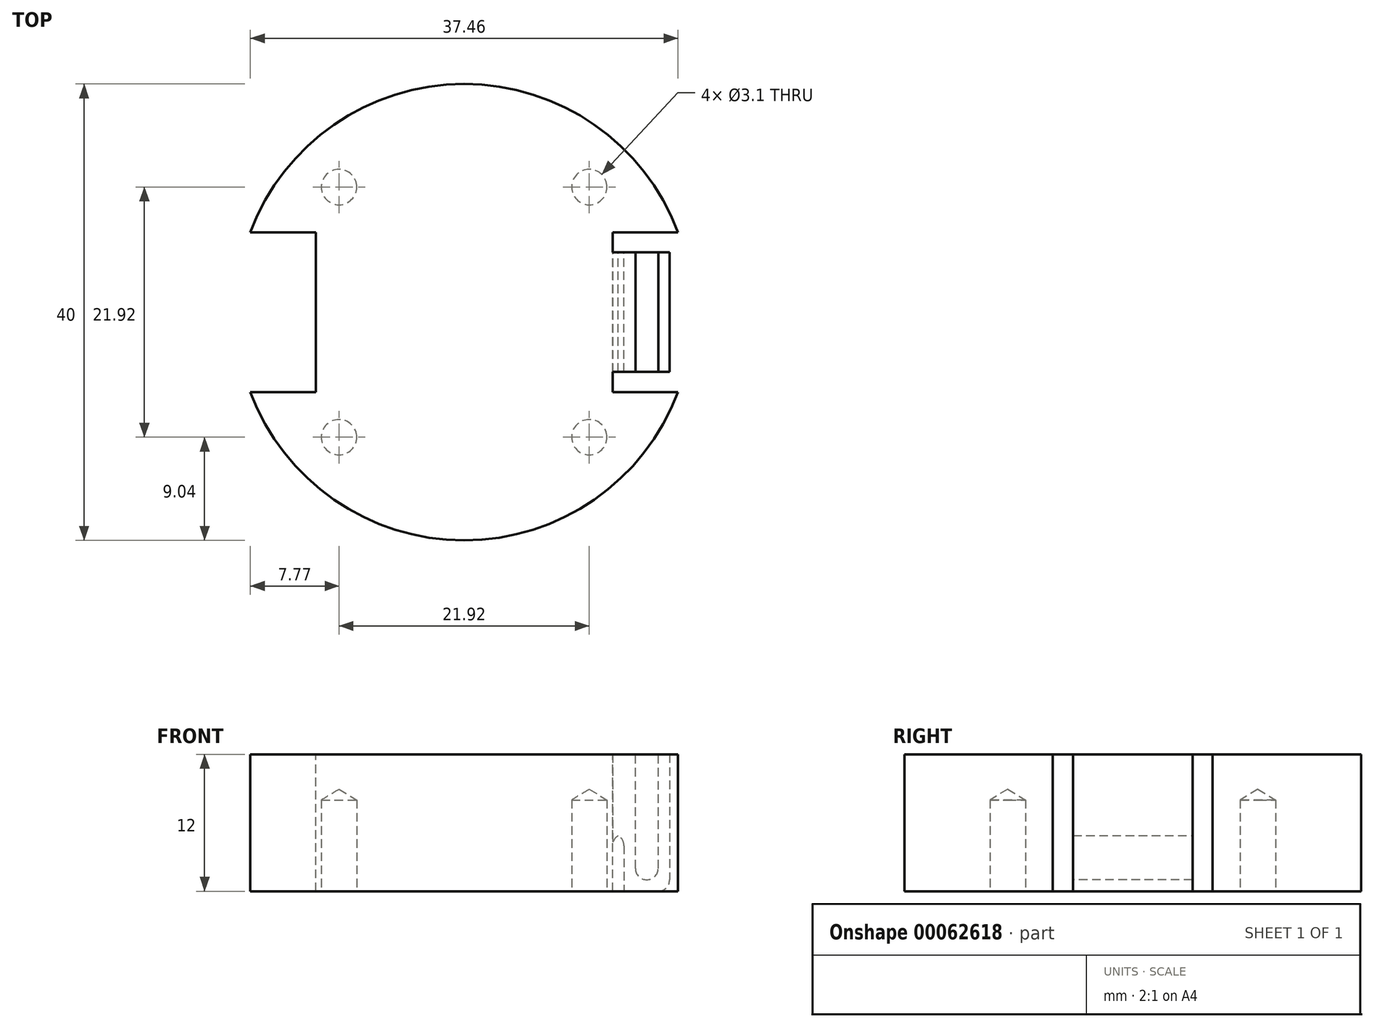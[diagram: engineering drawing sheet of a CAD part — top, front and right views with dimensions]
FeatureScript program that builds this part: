
annotation { "Feature Type Name" : "Feature", "Feature Type Description" : "" }
export const myFeature = defineFeature(function(context is Context, id is Id, definition is map)
    precondition{}
    {
        {
            var Q0;
            Q0=qCreatedBy(makeId("Top.planeOp"),FACE);
            var sketch = newSketch(context, id + "F0", { "sketchPlane" : qUnion([Q0])});
            skCircle(sketch, "E0", {"center": v(0, 0) * mm, "radius": 20 * mm});
            skSolve(sketch);
        }
        {
            var Q0;
            Q0=makeQuery(id+"F0.imprint","IMPRINT",FACE,{"disambiguationData":[TD([[makeQuery(id+"F0.imprint","IMPRINT",EDGE,{"derivedFrom":sQuery(id+"F0.wireOp",EDGE,"E0")}),1.0]])]});
            extrude(context, id + "F1", {"entities" : qUnion([Q0]), "depth" : 12 * mm});
        }
        {
            var Q0;
            Q0=makeQuery(id+"F1.opExtrude","CAP_FACE",FACE,{"disambiguationData":[OSD([sQuery(id+"F0.wireOp",EDGE,"E0")])],"isStart":true});
            var sketch = newSketch(context, id + "F2", { "sketchPlane" : qUnion([Q0])});
            skLineSegment(sketch, "E1", {"start": v(0, 0) * mm, "end": v(14.14, 14.14) * mm, "construction": true});
            skCircle(sketch, "E2.cCircle", {"center": v(0, 0) * mm, "radius": 15.5 * mm, "construction": true});
            skLineSegment(sketch, "E2.0", {"start": v(10.96, 10.96) * mm, "end": v(10.96, -10.96) * mm, "construction": true});
            skLineSegment(sketch, "E2.1", {"start": v(10.96, -10.96) * mm, "end": v(-10.96, -10.96) * mm, "construction": true});
            skLineSegment(sketch, "E2.2", {"start": v(-10.96, -10.96) * mm, "end": v(-10.96, 10.96) * mm, "construction": true});
            skLineSegment(sketch, "E2.3", {"start": v(-10.96, 10.96) * mm, "end": v(10.96, 10.96) * mm, "construction": true});
            skSolve(sketch);
        }
        {
            var Q0;
            Q0=sQuery(id+"F2.wireOp",VERTEX,"E2.3.start");
            var Q1;
            Q1=sQuery(id+"F2.wireOp",VERTEX,"E2.2.start");
            var Q2;
            Q2=sQuery(id+"F2.wireOp",VERTEX,"E2.1.start");
            var Q3;
            Q3=sQuery(id+"F2.wireOp",VERTEX,"E2.0.start");
            var Q4;
            Q4=makeQuery(id+"F1.opExtrude","SWEPT_BODY",BODY,{"disambiguationData":[OSD([sQuery(id+"F0.wireOp",EDGE,"E0")])]});
            hole(context, id + "F3", {"style" : HoleStyle.SIMPLE, "holeDiameter" : 3.1 * mm, "endStyle" : HoleEndStyle.BLIND, "holeDepth" : 8 * mm, "locations" : qUnion([Q0, Q1, Q2, Q3]), "scope" : qUnion([Q4])});
        }
        {
            var Q0;
            Q0=makeQuery(id+"F1.opExtrude","CAP_FACE",FACE,{"disambiguationData":[OSD([sQuery(id+"F0.wireOp",EDGE,"E0")])],"isStart":false});
            var sketch = newSketch(context, id + "F4", { "sketchPlane" : qUnion([Q0])});
            skLineSegment(sketch, "E3.rect.bottom", {"start": v(13, 7) * mm, "end": v(20, 7) * mm});
            skLineSegment(sketch, "E3.rect.top", {"start": v(13, -7) * mm, "end": v(20, -7) * mm});
            skLineSegment(sketch, "E3.rect.left", {"start": v(13, 7) * mm, "end": v(13, -7) * mm});
            skLineSegment(sketch, "E3.rect.right", {"start": v(20, 7) * mm, "end": v(20, -7) * mm});
            skPoint(sketch, "E3.rect.middle", {"position": v(16.5, 0) * mm});
            skLineSegment(sketch, "E4.rect.bottom", {"start": v(-13, 7) * mm, "end": v(-20, 7) * mm});
            skLineSegment(sketch, "E4.rect.top", {"start": v(-13, -7) * mm, "end": v(-20, -7) * mm});
            skLineSegment(sketch, "E4.rect.left", {"start": v(-13, 7) * mm, "end": v(-13, -7) * mm});
            skLineSegment(sketch, "E4.rect.right", {"start": v(-20, 7) * mm, "end": v(-20, -7) * mm});
            skPoint(sketch, "E4.rect.middle", {"position": v(-16.5, 0) * mm});
            skSolve(sketch);
        }
        {
            var Q0;
            {var subQ0=sQuery(id+"F4.wireOp",EDGE,"E3.rect.left");Q0=makeQuery(id+"F4.imprint","IMPRINT",FACE,{"disambiguationData":[TD([[makeQuery(id+"F4.imprint","IMPRINT",EDGE,{"derivedFrom":subQ0}),-1.0]])]});}
            extrude(context, id + "F5", {"entities" : qUnion([Q0]), "operationType" : NewBodyOperationType.INTERSECT, "endBound" : BoundingType.THROUGH_ALL, "oppositeDirection" : true, "depth" : 25 * mm});
        }
        {
            var Q0;
            Q0=qCreatedBy(makeId("Top.planeOp"),FACE);
            var sketch = newSketch(context, id + "F6", { "sketchPlane" : qUnion([Q0])});
            skLineSegment(sketch, "E5.rect.bottom", {"start": v(13, 5.23) * mm, "end": v(18, 5.23) * mm});
            skLineSegment(sketch, "E5.rect.top", {"start": v(13, -5.23) * mm, "end": v(18, -5.23) * mm});
            skLineSegment(sketch, "E5.rect.left", {"start": v(13, 5.23) * mm, "end": v(13, -5.23) * mm});
            skLineSegment(sketch, "E5.rect.right", {"start": v(18, 5.23) * mm, "end": v(18, -5.23) * mm});
            skPoint(sketch, "E5.rect.middle", {"position": v(15.5, 0) * mm});
            skSolve(sketch);
        }
        {
            var Q0;
            Q0=makeQuery(id+"F6.imprint","IMPRINT",FACE,{"disambiguationData":[TD([[makeQuery(id+"F6.imprint","IMPRINT",EDGE,{"derivedFrom":sQuery(id+"F6.wireOp",EDGE,"E5.rect.bottom")}),-1.0]])]});
            extrude(context, id + "F7", {"entities" : qUnion([Q0]), "operationType" : NewBodyOperationType.ADD, "depth" : 12 * mm});
        }
        {
            var Q0;
            {var subQ4=sQuery(id+"F4.wireOp",EDGE,"E3.rect.left");Q0=makeQuery(id+"F4.imprint","IMPRINT",FACE,{"disambiguationData":[TD([[makeQuery(id+"F4.imprint","IMPRINT",EDGE,{"derivedFrom":subQ4}),-1.0]])]});}
            var sketch = newSketch(context, id + "F8", { "sketchPlane" : qUnion([Q0])});
            skLineSegment(sketch, "E6.bottom", {"start": v(15, 5.23) * mm, "end": v(17, 5.23) * mm});
            skLineSegment(sketch, "E6.top", {"start": v(15, -5.23) * mm, "end": v(17, -5.23) * mm});
            skLineSegment(sketch, "E6.left", {"start": v(15, 5.23) * mm, "end": v(15, -5.23) * mm});
            skLineSegment(sketch, "E6.right", {"start": v(17, 5.23) * mm, "end": v(17, -5.23) * mm});
            skSolve(sketch);
        }
        {
            var Q0;
            Q0=makeQuery(id+"F8.imprint","IMPRINT",FACE,{"disambiguationData":[TD([[makeQuery(id+"F8.imprint","IMPRINT",EDGE,{"derivedFrom":sQuery(id+"F8.wireOp",EDGE,"E6.bottom")}),-1.0]])]});
            extrude(context, id + "F9", {"entities" : qUnion([Q0]), "operationType" : NewBodyOperationType.REMOVE, "oppositeDirection" : true, "depth" : 11 * mm});
        }
        {
            var Q0;
            Q0=qCreatedBy(makeId("Top.planeOp"),FACE);
            var sketch = newSketch(context, id + "F10", { "sketchPlane" : qUnion([Q0])});
            skLineSegment(sketch, "E7.bottom", {"start": v(13, -5.23) * mm, "end": v(14, -5.23) * mm});
            skLineSegment(sketch, "E7.top", {"start": v(13, 5.23) * mm, "end": v(14, 5.23) * mm});
            skLineSegment(sketch, "E7.left", {"start": v(13, -5.23) * mm, "end": v(13, 5.23) * mm});
            skLineSegment(sketch, "E7.right", {"start": v(14, -5.23) * mm, "end": v(14, 5.23) * mm});
            skSolve(sketch);
        }
        {
            var Q0;
            Q0 = qSketchRegion(id + "F10", true);
            extrude(context, id + "F11", {"entities" : qUnion([Q0]), "operationType" : NewBodyOperationType.REMOVE, "depth" : 5 * mm});
        }
        {
            var Q0;
            Q0=makeQuery(id+"F9.boolean.opBoolean","COPY",EDGE,{"derivedFrom":makeQuery(id+"F9.opExtrude","CAP_EDGE",EDGE,{"disambiguationData":[OSD([sQuery(id+"F8.wireOp",EDGE,"E6.left")])],"isStart":false})});
            var Q1;
            Q1=makeQuery(id+"F9.boolean.opBoolean","COPY",EDGE,{"derivedFrom":makeQuery(id+"F9.opExtrude","CAP_EDGE",EDGE,{"disambiguationData":[OSD([sQuery(id+"F8.wireOp",EDGE,"E6.right")])],"isStart":false})});
            var Q2;
            Q2=makeQuery(id+"F7.opExtrude","CAP_EDGE",EDGE,{"disambiguationData":[OSD([sQuery(id+"F6.wireOp",EDGE,"E5.rect.right")])],"isStart":true});
            var Q3;
            Q3=makeQuery(id+"F11.boolean.opBoolean","COPY",EDGE,{"derivedFrom":makeQuery(id+"F11.opExtrude","CAP_EDGE",EDGE,{"disambiguationData":[OSD([sQuery(id+"F10.wireOp",EDGE,"E7.right")])],"isStart":true})});
            var Q4;
            Q4=makeQuery(id+"F11.boolean.opBoolean","COPY",EDGE,{"derivedFrom":makeQuery(id+"F11.opExtrude","CAP_EDGE",EDGE,{"disambiguationData":[OSD([sQuery(id+"F10.wireOp",EDGE,"E7.right")])],"isStart":false})});
            var Q5;
            Q5=makeQuery(id+"F11.boolean.opBoolean","COPY",EDGE,{"derivedFrom":makeQuery(id+"F11.opExtrude","CAP_EDGE",EDGE,{"disambiguationData":[OSD([sQuery(id+"F10.wireOp",EDGE,"E7.left")])],"isStart":false})});
            fillet(context, id + "F12", {"entities" : qUnion([Q0, Q1, Q2, Q3, Q4, Q5]), "radius" : 1 * mm, "tangentPropagation" : true, "allowEdgeOverflow" : false});
        }
    });
